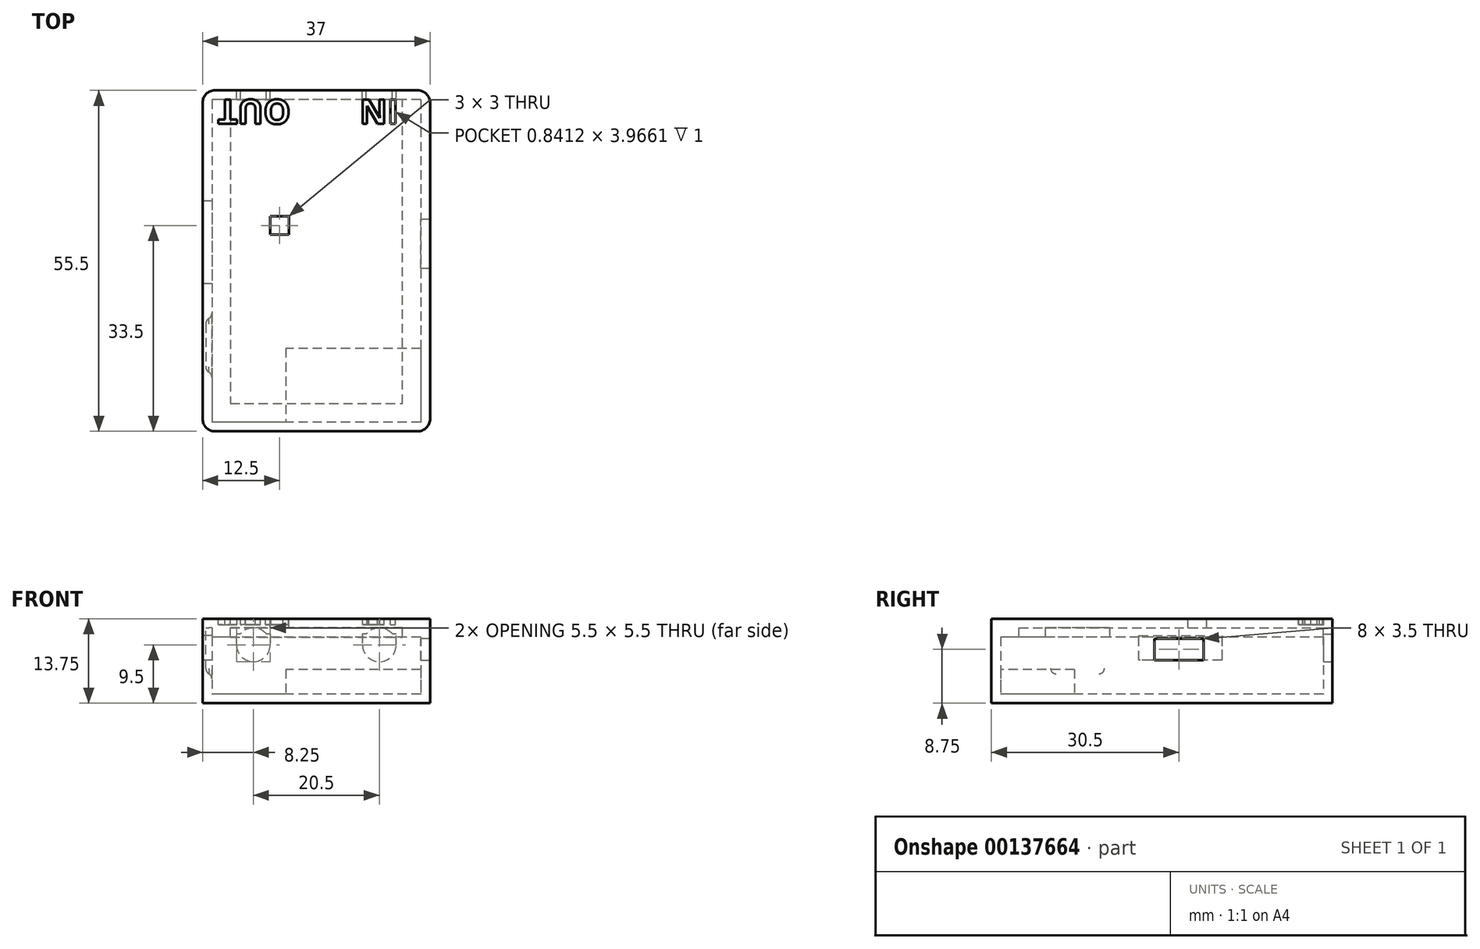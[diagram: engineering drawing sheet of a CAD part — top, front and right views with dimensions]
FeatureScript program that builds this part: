
annotation { "Feature Type Name" : "Feature", "Feature Type Description" : "" }
export const myFeature = defineFeature(function(context is Context, id is Id, definition is map)
    precondition{}
    {
        {
            var Q0;
            Q0=qCreatedBy(makeId("Top.planeOp"),FACE);
            var sketch = newSketch(context, id + "F0", { "sketchPlane" : qUnion([Q0])});
            skLineSegment(sketch, "E0.bottom", {"start": v(17, 26.25) * mm, "end": v(-17, 26.25) * mm});
            skLineSegment(sketch, "E0.top", {"start": v(17, -26.25) * mm, "end": v(-17, -26.25) * mm});
            skLineSegment(sketch, "E0.left", {"start": v(17, 26.25) * mm, "end": v(17, -26.25) * mm});
            skLineSegment(sketch, "E0.right", {"start": v(-17, 26.25) * mm, "end": v(-17, -26.25) * mm});
            skPoint(sketch, "E0.middle", {"position": v(0, 0) * mm});
            skPoint(sketch, "E1", {"position": v(13, 26.25) * mm});
            skPoint(sketch, "E2", {"position": v(7.5, 26.25) * mm});
            skPoint(sketch, "E3", {"position": v(-7.5, 26.25) * mm});
            skPoint(sketch, "E4", {"position": v(-13, 26.25) * mm});
            skPoint(sketch, "E5", {"position": v(-17, -3.75) * mm});
            skPoint(sketch, "E6", {"position": v(-17, 9.75) * mm});
            skPoint(sketch, "E7", {"position": v(17, -1.25) * mm});
            skPoint(sketch, "E8", {"position": v(17, 6.75) * mm});
            skPoint(sketch, "E9", {"position": v(-6, 5.75) * mm});
            skLineSegment(sketch, "E10.bottom", {"start": v(-7.5, 7.25) * mm, "end": v(-4.5, 7.25) * mm});
            skLineSegment(sketch, "E10.top", {"start": v(-7.5, 4.25) * mm, "end": v(-4.5, 4.25) * mm});
            skLineSegment(sketch, "E10.left", {"start": v(-7.5, 7.25) * mm, "end": v(-7.5, 4.25) * mm});
            skLineSegment(sketch, "E10.right", {"start": v(-4.5, 7.25) * mm, "end": v(-4.5, 4.25) * mm});
            skSolve(sketch);
        }
        {
            var Q0;
            Q0=qCreatedBy(makeId("Top.planeOp"),FACE);
            var sketch = newSketch(context, id + "F1", { "sketchPlane" : qUnion([Q0])});
            skLineSegment(sketch, "E11.0", {"start": v(-18.5, 27.75) * mm, "end": v(-18.5, -27.75) * mm});
            skLineSegment(sketch, "E11.1", {"start": v(18.5, 27.75) * mm, "end": v(-18.5, 27.75) * mm});
            skLineSegment(sketch, "E11.2", {"start": v(18.5, 27.75) * mm, "end": v(18.5, -27.75) * mm});
            skLineSegment(sketch, "E11.3", {"start": v(18.5, -27.75) * mm, "end": v(-18.5, -27.75) * mm});
            skSolve(sketch);
        }
        {
            var Q0;
            Q0 = qSketchRegion(id + "F1", true);
            extrude(context, id + "F2", {"entities" : qUnion([Q0]), "depth" : (13.5 - 1.25) * mm});
        }
        {
            var Q0;
            Q0=makeQuery(id+"F2.opExtrude","CAP_FACE",FACE,{"disambiguationData":[OSD([sQuery(id+"F1.wireOp",EDGE,"E11.0"),sQuery(id+"F1.wireOp",EDGE,"E11.1"),sQuery(id+"F1.wireOp",EDGE,"E11.2"),sQuery(id+"F1.wireOp",EDGE,"E11.3")])],"isStart":false});
            shell(context, id + "F3", {"entities" : qUnion([Q0]), "thickness" : 1.5 * mm});
        }
        {
            var Q0;
            Q0=qCreatedBy(makeId("Top.planeOp"),FACE);
            cPlane(context, id + "F4", {"entities" : qUnion([Q0]), "cplaneType" : CPlaneType.OFFSET, "offset" : 5.5 * mm, "width" : 150 * mm, "height" : 150 * mm});
        }
        {
            var Q0;
            Q0=makeQuery(id+"F3.opShell","OFFSET_FACE",FACE,{"disambiguationData":[OSD([sQuery(id+"F1.wireOp",EDGE,"E11.0"),sQuery(id+"F1.wireOp",EDGE,"E11.1"),sQuery(id+"F1.wireOp",EDGE,"E11.2"),sQuery(id+"F1.wireOp",EDGE,"E11.3")])]});
            var sketch = newSketch(context, id + "F5", { "sketchPlane" : qUnion([Q0])});
            skLineSegment(sketch, "E12", {"start": v(-5, -26.25) * mm, "end": v(17, -26.25) * mm});
            skLineSegment(sketch, "E13", {"start": v(17, -26.25) * mm, "end": v(17, -14.25) * mm});
            skLineSegment(sketch, "E14", {"start": v(17, -14.25) * mm, "end": v(-5, -14.25) * mm});
            skLineSegment(sketch, "E15", {"start": v(-5, -14.25) * mm, "end": v(-5, -26.25) * mm});
            skSolve(sketch);
        }
        {
            var Q0;
            Q0 = qSketchRegion(id + "F5", true);
            var Q1;
            Q1=qCreatedBy(id+"F4.planeOp",FACE);
            extrude(context, id + "F6", {"entities" : qUnion([Q0]), "operationType" : NewBodyOperationType.ADD, "endBound" : BoundingType.UP_TO_SURFACE, "endBoundEntityFace" : qUnion([Q1]), "depth" : 4 * mm});
        }
        {
            var Q0;
            Q0=makeQuery(id+"F2.opExtrude","SWEPT_FACE",FACE,{"disambiguationData":[OSD([sQuery(id+"F1.wireOp",EDGE,"E11.0")])]});
            var sketch = newSketch(context, id + "F7", { "sketchPlane" : qUnion([Q0])});
            skPoint(sketch, "E16.0", {"position": v(-9.75, 0) * mm});
            skPoint(sketch, "E16.1", {"position": v(3.75, 0) * mm});
            skLineSegment(sketch, "E17", {"start": v(-9.75, 7) * mm, "end": v(3.75, 7) * mm});
            skLineSegment(sketch, "E18", {"start": v(3.75, 7) * mm, "end": v(3.75, 11) * mm});
            skLineSegment(sketch, "E19", {"start": v(3.75, 11) * mm, "end": v(-9.75, 11) * mm});
            skLineSegment(sketch, "E20", {"start": v(-9.75, 11) * mm, "end": v(-9.75, 7) * mm});
            skSolve(sketch);
        }
        {
            var Q0;
            Q0 = qSketchRegion(id + "F7", true);
            var Q1;
            Q1=makeQuery(id+"F3.opShell","OFFSET_FACE",FACE,{"disambiguationData":[OSD([sQuery(id+"F1.wireOp",EDGE,"E11.0")])]});
            extrude(context, id + "F8", {"entities" : qUnion([Q0]), "operationType" : NewBodyOperationType.REMOVE, "endBound" : BoundingType.UP_TO_SURFACE, "oppositeDirection" : true, "endBoundEntityFace" : qUnion([Q1]), "depth" : 25 * mm});
        }
        {
            var Q0;
            Q0=makeQuery(id+"F2.opExtrude","SWEPT_FACE",FACE,{"disambiguationData":[OSD([sQuery(id+"F1.wireOp",EDGE,"E11.2")])]});
            var sketch = newSketch(context, id + "F9", { "sketchPlane" : qUnion([Q0])});
            skPoint(sketch, "E21.0", {"position": v(-1.25, 0) * mm});
            skPoint(sketch, "E21.1", {"position": v(6.75, 0) * mm});
            skLineSegment(sketch, "E22", {"start": v(-1.25, 7) * mm, "end": v(6.75, 7) * mm});
            skLineSegment(sketch, "E23", {"start": v(6.75, 7) * mm, "end": v(6.75, 13.5) * mm});
            skLineSegment(sketch, "E24", {"start": v(6.75, 13.5) * mm, "end": v(-1.25, 13.5) * mm});
            skLineSegment(sketch, "E25", {"start": v(-1.25, 13.5) * mm, "end": v(-1.25, 7) * mm});
            skSolve(sketch);
        }
        {
            var Q0;
            Q0 = qSketchRegion(id + "F9", true);
            var Q1;
            Q1=makeQuery(id+"F3.opShell","OFFSET_FACE",FACE,{"disambiguationData":[OSD([sQuery(id+"F1.wireOp",EDGE,"E11.2")])]});
            extrude(context, id + "F10", {"entities" : qUnion([Q0]), "operationType" : NewBodyOperationType.REMOVE, "endBound" : BoundingType.UP_TO_SURFACE, "oppositeDirection" : true, "endBoundEntityFace" : qUnion([Q1]), "depth" : 25 * mm});
        }
        {
            var Q0;
            Q0=makeQuery(id+"F2.opExtrude","SWEPT_FACE",FACE,{"disambiguationData":[OSD([sQuery(id+"F1.wireOp",EDGE,"E11.1")])]});
            var sketch = newSketch(context, id + "F11", { "sketchPlane" : qUnion([Q0])});
            skPoint(sketch, "E26.0", {"position": v(-13, 0) * mm});
            skPoint(sketch, "E26.1", {"position": v(-7.5, 0) * mm});
            skPoint(sketch, "E26.2", {"position": v(7.5, 0) * mm});
            skPoint(sketch, "E26.3", {"position": v(13, 0) * mm});
            skLineSegment(sketch, "E27", {"start": v(-13, 9.5) * mm, "end": v(-7.5, 9.5) * mm, "construction": true});
            skLineSegment(sketch, "E28", {"start": v(-10.25, 5.5) * mm, "end": v(-10.25, 12.25) * mm, "construction": true});
            skPoint(sketch, "E28.startSnap0", {"position": v(-10.25, 9.5) * mm});
            skLineSegment(sketch, "E29", {"start": v(-13, 9.5) * mm, "end": v(-13, 12.25) * mm});
            skLineSegment(sketch, "E30", {"start": v(-13, 12.25) * mm, "end": v(-7.5, 12.25) * mm});
            skLineSegment(sketch, "E31", {"start": v(-7.5, 12.25) * mm, "end": v(-7.5, 9.5) * mm});
            skArc(sketch, "E32", {"start": v(-13, 9.5) * mm, "mid": v(-10.25, 6.75) * mm, "end": v(-7.5, 9.5) * mm});
            skArc(sketch, "E33", {"start": v(-7.5, 9.5) * mm, "mid": v(-10.25, 12.25) * mm, "end": v(-13, 9.5) * mm, "construction": true});
            skLineSegment(sketch, "E34.MirrorCS", {"start": v(13, 9.5) * mm, "end": v(13, 12.25) * mm});
            skLineSegment(sketch, "E35.MirrorCS", {"start": v(7.5, 12.25) * mm, "end": v(7.5, 9.5) * mm});
            skLineSegment(sketch, "E36.MirrorCS", {"start": v(13, 12.25) * mm, "end": v(7.5, 12.25) * mm});
            skArc(sketch, "E37.MirrorCS", {"start": v(13, 9.5) * mm, "mid": v(10.25, 6.75) * mm, "end": v(7.5, 9.5) * mm});
            skArc(sketch, "E38.MirrorCS", {"start": v(7.5, 9.5) * mm, "mid": v(10.25, 12.25) * mm, "end": v(13, 9.5) * mm, "construction": true});
            skSolve(sketch);
        }
        {
            var Q0;
            Q0 = qSketchRegion(id + "F11", true);
            var Q1;
            Q1=makeQuery(id+"F3.opShell","OFFSET_FACE",FACE,{"disambiguationData":[OSD([sQuery(id+"F1.wireOp",EDGE,"E11.1")])]});
            extrude(context, id + "F12", {"entities" : qUnion([Q0]), "operationType" : NewBodyOperationType.REMOVE, "endBound" : BoundingType.UP_TO_SURFACE, "oppositeDirection" : true, "endBoundEntityFace" : qUnion([Q1]), "depth" : 25 * mm});
        }
        {
            var Q0;
            Q0=makeQuery(id+"F2.opExtrude","SWEPT_EDGE",EDGE,{"disambiguationData":[OSD([sQuery(id+"F1.wireOp",EDGE,"E11.0"),sQuery(id+"F1.wireOp",EDGE,"E11.1")])]});
            var Q1;
            Q1=makeQuery(id+"F2.opExtrude","SWEPT_EDGE",EDGE,{"disambiguationData":[OSD([sQuery(id+"F1.wireOp",EDGE,"E11.1"),sQuery(id+"F1.wireOp",EDGE,"E11.2")])]});
            var Q2;
            Q2=makeQuery(id+"F2.opExtrude","SWEPT_EDGE",EDGE,{"disambiguationData":[OSD([sQuery(id+"F1.wireOp",EDGE,"E11.0"),sQuery(id+"F1.wireOp",EDGE,"E11.3")])]});
            var Q3;
            Q3=makeQuery(id+"F2.opExtrude","SWEPT_EDGE",EDGE,{"disambiguationData":[OSD([sQuery(id+"F1.wireOp",EDGE,"E11.2"),sQuery(id+"F1.wireOp",EDGE,"E11.3")])]});
            fillet(context, id + "F13", {"entities" : qUnion([Q0, Q1, Q2, Q3]), "radius" : 2 * mm, "tangentPropagation" : true, "allowEdgeOverflow" : false});
        }
        {
            var Q0;
            {var subQ0=sQuery(id+"F1.wireOp",EDGE,"E11.2");var subQ1=sQuery(id+"F1.wireOp",EDGE,"E11.3");var subQ2=sQuery(id+"F1.wireOp",EDGE,"E11.1");var subQ3=sQuery(id+"F1.wireOp",EDGE,"E11.0");Q0=makeQuery(id+"F12.boolean.opBoolean","SPLIT",FACE,{"disambiguationData":[TD([makeQuery(id+"F2.opExtrude","SWEPT_FACE",FACE,{"disambiguationData":[OSD([subQ3])]})])],"derivedFrom":makeQuery(id+"F2.opExtrude","CAP_FACE",FACE,{"disambiguationData":[OSD([subQ3,subQ2,subQ0,subQ1])],"isStart":false})});}
            var sketch = newSketch(context, id + "F14", { "sketchPlane" : qUnion([Q0])});
            skLineSegment(sketch, "E39", {"start": v(-17, -18.25) * mm, "end": v(-17, -9.25) * mm});
            skLineSegment(sketch, "E40", {"start": v(-17, -9.25) * mm, "end": v(-17, -9.25) * mm});
            skLineSegment(sketch, "E41", {"start": v(-18, -10.25) * mm, "end": v(-18, -17.25) * mm});
            skLineSegment(sketch, "E42", {"start": v(-17, -18.25) * mm, "end": v(-17, -18.25) * mm});
            skPoint(sketch, "E43.visualSharp", {"position": v(-18, -18.25) * mm});
            skArc(sketch, "E43.filletArc", {"start": v(-18, -17.25) * mm, "mid": v(-17.7, -17.96) * mm, "end": v(-17, -18.25) * mm});
            skPoint(sketch, "E44.visualSharp", {"position": v(-18, -9.25) * mm});
            skArc(sketch, "E44.filletArc", {"start": v(-17, -9.25) * mm, "mid": v(-17.7, -9.54) * mm, "end": v(-18, -10.25) * mm});
            skSolve(sketch);
        }
        {
            var Q0;
            Q0 = qSketchRegion(id + "F14", true);
            extrude(context, id + "F15", {"entities" : qUnion([Q0]), "operationType" : NewBodyOperationType.REMOVE, "oppositeDirection" : true, "depth" : 7.6 * mm});
        }
        {
            var Q0;
            Q0=makeQuery(id+"F15.boolean.opBoolean","COPY",EDGE,{"derivedFrom":makeQuery(id+"F15.opExtrude","CAP_EDGE",EDGE,{"disambiguationData":[OSD([sQuery(id+"F14.wireOp",EDGE,"E41")])],"isStart":false})});
            fillet(context, id + "F16", {"entities" : qUnion([Q0]), "radius" : 1 * mm, "tangentPropagation" : true, "allowEdgeOverflow" : false});
        }
        {
            var Q0;
            Q0=makeQuery(id+"F16.opFillet","BLEND_EDGE",EDGE,{"blendedFrom":[makeQuery(id+"F15.boolean.opBoolean","COPY",EDGE,{"derivedFrom":makeQuery(id+"F15.opExtrude","CAP_EDGE",EDGE,{"disambiguationData":[OSD([sQuery(id+"F14.wireOp",EDGE,"E41")])],"isStart":false})}),makeQuery(id+"F3.opShell","OFFSET_FACE",FACE,{"disambiguationData":[OSD([sQuery(id+"F1.wireOp",EDGE,"E11.0")])]})],"blendedInto":[makeQuery(id+"F3.opShell","OFFSET_FACE",FACE,{"disambiguationData":[OSD([sQuery(id+"F1.wireOp",EDGE,"E11.0")])]})]});
            fillet(context, id + "F17", {"entities" : qUnion([Q0]), "radius" : 1 * mm, "tangentPropagation" : true, "allowEdgeOverflow" : false});
        }
        {
            var Q0;
            {var subQ0=sQuery(id+"F1.wireOp",EDGE,"E11.2");var subQ1=sQuery(id+"F1.wireOp",EDGE,"E11.3");var subQ2=sQuery(id+"F1.wireOp",EDGE,"E11.1");var subQ3=sQuery(id+"F1.wireOp",EDGE,"E11.0");Q0=makeQuery(id+"F12.boolean.opBoolean","SPLIT",FACE,{"disambiguationData":[TD([makeQuery(id+"F2.opExtrude","SWEPT_FACE",FACE,{"disambiguationData":[OSD([subQ3])]})])],"derivedFrom":makeQuery(id+"F2.opExtrude","CAP_FACE",FACE,{"disambiguationData":[OSD([subQ3,subQ2,subQ0,subQ1])],"isStart":false})});}
            var sketch = newSketch(context, id + "F18", { "sketchPlane" : qUnion([Q0])});
            skArc(sketch, "E45.0", {"start": v(-16.5, 27.75) * mm, "mid": v(-17.91, 27.16) * mm, "end": v(-18.5, 25.75) * mm});
            skLineSegment(sketch, "E45.1", {"start": v(-18.5, 25.75) * mm, "end": v(-18.5, -25.75) * mm});
            skLineSegment(sketch, "E45.5", {"start": v(16.5, -27.75) * mm, "end": v(-16.5, -27.75) * mm});
            skArc(sketch, "E45.6", {"start": v(-18.5, -25.75) * mm, "mid": v(-17.91, -27.16) * mm, "end": v(-16.5, -27.75) * mm});
            skLineSegment(sketch, "E46", {"start": v(-16.5, 27.75) * mm, "end": v(16.5, 27.75) * mm});
            skArc(sketch, "E47.0", {"start": v(16.5, -27.75) * mm, "mid": v(17.91, -27.16) * mm, "end": v(18.5, -25.75) * mm});
            skArc(sketch, "E47.1", {"start": v(18.5, 25.75) * mm, "mid": v(17.91, 27.16) * mm, "end": v(16.5, 27.75) * mm});
            skLineSegment(sketch, "E48", {"start": v(18.5, 25.75) * mm, "end": v(18.5, -25.75) * mm});
            skSolve(sketch);
        }
        {
            var Q0;
            Q0 = qSketchRegion(id + "F18", true);
            extrude(context, id + "F19", {"entities" : qUnion([Q0]), "depth" : 1.5 * mm});
        }
        {
            var Q0;
            Q0=makeQuery(id+"F19.opExtrude","SWEPT_FACE",FACE,{"disambiguationData":[OSD([sQuery(id+"F18.wireOp",EDGE,"E46")])]});
            var sketch = newSketch(context, id + "F20", { "sketchPlane" : qUnion([Q0])});
            skArc(sketch, "E49.0", {"start": v(-7.5, 9.5) * mm, "mid": v(-7.66, 10.43) * mm, "end": v(-8.13, 11.25) * mm, "construction": true});
            skLineSegment(sketch, "E49.1", {"start": v(-13, 9.5) * mm, "end": v(-13, 11.25) * mm, "construction": true});
            skLineSegment(sketch, "E49.2", {"start": v(-7.5, 12.25) * mm, "end": v(-7.5, 11.25) * mm});
            skLineSegment(sketch, "E49.3", {"start": v(-13, 12.25) * mm, "end": v(-7.5, 12.25) * mm});
            skLineSegment(sketch, "E49.4", {"start": v(7.5, 12.25) * mm, "end": v(7.5, 11.25) * mm});
            skArc(sketch, "E49.5", {"start": v(7.5, 9.5) * mm, "mid": v(7.66, 10.43) * mm, "end": v(8.13, 11.25) * mm, "construction": true});
            skLineSegment(sketch, "E49.6", {"start": v(13, 9.5) * mm, "end": v(13, 11.25) * mm, "construction": true});
            skLineSegment(sketch, "E49.7", {"start": v(13, 12.25) * mm, "end": v(7.5, 12.25) * mm});
            skLineSegment(sketch, "E50", {"start": v(-13, 11.25) * mm, "end": v(-12.37, 11.25) * mm});
            skPoint(sketch, "E51", {"position": v(-12.37, 11.25) * mm});
            skLineSegment(sketch, "E52.trimOffspring", {"start": v(-8.13, 11.25) * mm, "end": v(-7.5, 11.25) * mm});
            skLineSegment(sketch, "E53.trimOffspring", {"start": v(7.5, 11.25) * mm, "end": v(8.13, 11.25) * mm});
            skLineSegment(sketch, "E54.trimOffspring", {"start": v(12.37, 11.25) * mm, "end": v(12.37, 11.25) * mm});
            skArc(sketch, "E55", {"start": v(-12.37, 11.25) * mm, "mid": v(-12.84, 10.43) * mm, "end": v(-13, 9.5) * mm, "construction": true});
            skLineSegment(sketch, "E56", {"start": v(-13, 11.25) * mm, "end": v(-13, 12.25) * mm});
            skLineSegment(sketch, "E57", {"start": v(-7.5, 11.25) * mm, "end": v(-7.5, 9.5) * mm, "construction": true});
            skArc(sketch, "E58", {"start": v(-8.13, 11.25) * mm, "mid": v(-10.25, 12.25) * mm, "end": v(-12.37, 11.25) * mm});
            skArc(sketch, "E59", {"start": v(8.13, 11.25) * mm, "mid": v(10.25, 12.25) * mm, "end": v(12.37, 11.25) * mm});
            skLineSegment(sketch, "E60", {"start": v(7.5, 11.25) * mm, "end": v(7.5, 9.5) * mm, "construction": true});
            skLineSegment(sketch, "E61", {"start": v(12.37, 11.25) * mm, "end": v(13, 11.25) * mm});
            skLineSegment(sketch, "E62", {"start": v(13, 11.25) * mm, "end": v(13, 12.25) * mm});
            skArc(sketch, "E63", {"start": v(12.37, 11.25) * mm, "mid": v(12.84, 10.43) * mm, "end": v(13, 9.5) * mm, "construction": true});
            skSolve(sketch);
        }
        {
            var Q0;
            Q0 = qSketchRegion(id + "F20", true);
            var Q1;
            Q1=makeQuery(id+"F3.opShell","OFFSET_FACE",FACE,{"disambiguationData":[OSD([sQuery(id+"F1.wireOp",EDGE,"E11.1")])]});
            extrude(context, id + "F21", {"entities" : qUnion([Q0]), "operationType" : NewBodyOperationType.ADD, "endBound" : BoundingType.UP_TO_SURFACE, "oppositeDirection" : true, "endBoundEntityFace" : qUnion([Q1]), "depth" : 25 * mm});
        }
        {
            var Q0;
            Q0=makeQuery(id+"F19.opExtrude","CAP_FACE",FACE,{"disambiguationData":[OSD([sQuery(id+"F18.wireOp",EDGE,"E45.0"),sQuery(id+"F18.wireOp",EDGE,"E45.1"),sQuery(id+"F18.wireOp",EDGE,"E45.2"),sQuery(id+"F18.wireOp",EDGE,"E45.3"),sQuery(id+"F18.wireOp",EDGE,"E45.4"),sQuery(id+"F18.wireOp",EDGE,"E45.5"),sQuery(id+"F18.wireOp",EDGE,"E45.6"),sQuery(id+"F18.wireOp",EDGE,"E46")])],"isStart":true});
            var sketch = newSketch(context, id + "F22", { "sketchPlane" : qUnion([Q0])});
            skLineSegment(sketch, "E64.0", {"start": v(17, -26.25) * mm, "end": v(17, 26.25) * mm});
            skLineSegment(sketch, "E64.1", {"start": v(17, 26.25) * mm, "end": v(-17, 26.25) * mm});
            skLineSegment(sketch, "E64.2", {"start": v(-17, -26.25) * mm, "end": v(-17, 26.25) * mm});
            skLineSegment(sketch, "E65", {"start": v(-14, -26.25) * mm, "end": v(-17, -26.25) * mm});
            skLineSegment(sketch, "E66", {"start": v(-14, -26.25) * mm, "end": v(-14, 23.25) * mm});
            skLineSegment(sketch, "E67", {"start": v(14, -26.25) * mm, "end": v(17, -26.25) * mm});
            skLineSegment(sketch, "E68", {"start": v(-14, 23.25) * mm, "end": v(14, 23.25) * mm});
            skLineSegment(sketch, "E69", {"start": v(14, 23.25) * mm, "end": v(14, -26.25) * mm});
            skSolve(sketch);
        }
        {
            var Q0;
            Q0 = qSketchRegion(id + "F22", true);
            extrude(context, id + "F23", {"entities" : qUnion([Q0]), "operationType" : NewBodyOperationType.ADD, "depth" : 1.5 * mm});
        }
        {
            var Q0;
            Q0=makeQuery(id+"F19.opExtrude","CAP_FACE",FACE,{"disambiguationData":[OSD([sQuery(id+"F18.wireOp",EDGE,"E45.0"),sQuery(id+"F18.wireOp",EDGE,"E45.1"),sQuery(id+"F18.wireOp",EDGE,"E45.2"),sQuery(id+"F18.wireOp",EDGE,"E45.3"),sQuery(id+"F18.wireOp",EDGE,"E45.4"),sQuery(id+"F18.wireOp",EDGE,"E45.5"),sQuery(id+"F18.wireOp",EDGE,"E45.6"),sQuery(id+"F18.wireOp",EDGE,"E46")])],"isStart":false});
            var sketch = newSketch(context, id + "F24", { "sketchPlane" : qUnion([Q0])});
            skLineSegment(sketch, "E70.0", {"start": v(-7.5, 7.25) * mm, "end": v(-4.5, 7.25) * mm});
            skLineSegment(sketch, "E70.1", {"start": v(-7.5, 7.25) * mm, "end": v(-7.5, 4.25) * mm});
            skLineSegment(sketch, "E70.2", {"start": v(-7.5, 4.25) * mm, "end": v(-4.5, 4.25) * mm});
            skLineSegment(sketch, "E70.3", {"start": v(-4.5, 7.25) * mm, "end": v(-4.5, 4.25) * mm});
            skSolve(sketch);
        }
        {
            var Q0;
            Q0 = qSketchRegion(id + "F24", true);
            var Q1;
            Q1=makeQuery(id+"F19.opExtrude","CAP_FACE",FACE,{"disambiguationData":[OSD([sQuery(id+"F18.wireOp",EDGE,"E45.0"),sQuery(id+"F18.wireOp",EDGE,"E45.1"),sQuery(id+"F18.wireOp",EDGE,"E45.2"),sQuery(id+"F18.wireOp",EDGE,"E45.3"),sQuery(id+"F18.wireOp",EDGE,"E45.4"),sQuery(id+"F18.wireOp",EDGE,"E45.5"),sQuery(id+"F18.wireOp",EDGE,"E45.6"),sQuery(id+"F18.wireOp",EDGE,"E46")])],"isStart":true});
            extrude(context, id + "F25", {"entities" : qUnion([Q0]), "operationType" : NewBodyOperationType.REMOVE, "endBound" : BoundingType.UP_TO_SURFACE, "oppositeDirection" : true, "endBoundEntityFace" : qUnion([Q1]), "depth" : 25 * mm});
        }
        {
            var Q0;
            Q0=makeQuery(id+"FsXd5NHJAuveMzu_2.boolean.opBoolean","MERGE",FACE,{"derivedFrom":[makeQuery(id+"F23.opExtrude","SWEPT_FACE",FACE,{"disambiguationData":[OSD([sQuery(id+"F22.wireOp",EDGE,"E64.0")])]}),makeQuery(id+"FsXd5NHJAuveMzu_2.opExtrude","SWEPT_FACE",FACE,{"disambiguationData":[OSD([sQuery(id+"FbdMCeF7yk2N0NU_2.wireOp",EDGE,"cKBC9f4m-p0WT-Iw1W-Nm8o-Yrg2UBetpT2z")])]})]});
            var sketch = newSketch(context, id + "F26", { "sketchPlane" : qUnion([Q0])});
            skLineSegment(sketch, "E71.0", {"start": v(-1.25, 12.25) * mm, "end": v(-1.25, 10.5) * mm});
            skLineSegment(sketch, "E71.2", {"start": v(6.75, 12.25) * mm, "end": v(-1.25, 12.25) * mm});
            skPoint(sketch, "E72.orphan", {"position": v(-1.25, 7) * mm});
            skPoint(sketch, "E73.orphan", {"position": v(6.75, 7) * mm});
            skPoint(sketch, "E71.1.end.orphan", {"position": v(6.75, 12.25) * mm});
            skPoint(sketch, "E74.orphan", {"position": v(25.75, 12.25) * mm});
            skPoint(sketch, "E75.orphan", {"position": v(-25.75, 12.25) * mm});
            skLineSegment(sketch, "E76.0", {"start": v(6.75, 10.5) * mm, "end": v(6.75, 12.25) * mm});
            skLineSegment(sketch, "E77.0", {"start": v(-1.25, 10.5) * mm, "end": v(6.75, 10.5) * mm});
            skSolve(sketch);
        }
        {
            var Q0;
            Q0 = qSketchRegion(id + "F26", true);
            var Q1;
            Q1=makeQuery(id+"F2.opExtrude","SWEPT_FACE",FACE,{"disambiguationData":[OSD([sQuery(id+"F1.wireOp",EDGE,"E11.2")])]});
            extrude(context, id + "F27", {"entities" : qUnion([Q0]), "operationType" : NewBodyOperationType.ADD, "endBound" : BoundingType.UP_TO_SURFACE, "endBoundEntityFace" : qUnion([Q1]), "depth" : 25 * mm});
        }
        {
            var Q0;
            Q0=makeQuery(id+"F19.opExtrude","CAP_FACE",FACE,{"disambiguationData":[OSD([sQuery(id+"F18.wireOp",EDGE,"E45.0"),sQuery(id+"F18.wireOp",EDGE,"E45.1"),sQuery(id+"F18.wireOp",EDGE,"E45.5"),sQuery(id+"F18.wireOp",EDGE,"E45.6"),sQuery(id+"F18.wireOp",EDGE,"E46"),sQuery(id+"F18.wireOp",EDGE,"E47.0"),sQuery(id+"F18.wireOp",EDGE,"E47.1"),sQuery(id+"F18.wireOp",EDGE,"E48")])],"isStart":false});
            var sketch = newSketch(context, id + "F28", { "sketchPlane" : qUnion([Q0])});
            skLineSegment(sketch, "E78.0", {"start": v(7.5, 27.75) * mm, "end": v(13, 27.75) * mm, "construction": true});
            skText(sketch, "E79", { "text": "IN", "fontName": "OpenSans-Bold.ttf"});
            skText(sketch, "E80", { "text": "OUT", "fontName": "OpenSans-Bold.ttf"});
            skLineSegment(sketch, "E81", {"start": v(10.25, 27.75) * mm, "end": v(10.25, 26.25) * mm, "construction": true});
            skLineSegment(sketch, "E82.0", {"start": v(-7.5, 27.75) * mm, "end": v(-13, 27.75) * mm, "construction": true});
            skLineSegment(sketch, "E83", {"start": v(-10.25, 27.75) * mm, "end": v(-10.25, 26.25) * mm, "construction": true});
            const initialGuessF28  = {"E79": [0.01336, 0.02625, -1, 0, 0.004], "E80": [-0.0042, 0.02625, -1, 0, 0.004]};
            skSetInitialGuess(sketch, initialGuessF28);
            skSolve(sketch);
        }
        {
            var Q0;
            Q0 = qSketchRegion(id + "F28", true);
            extrude(context, id + "F29", {"entities" : qUnion([Q0]), "operationType" : NewBodyOperationType.REMOVE, "oppositeDirection" : true, "depth" : 1 * mm});
        }
    });
